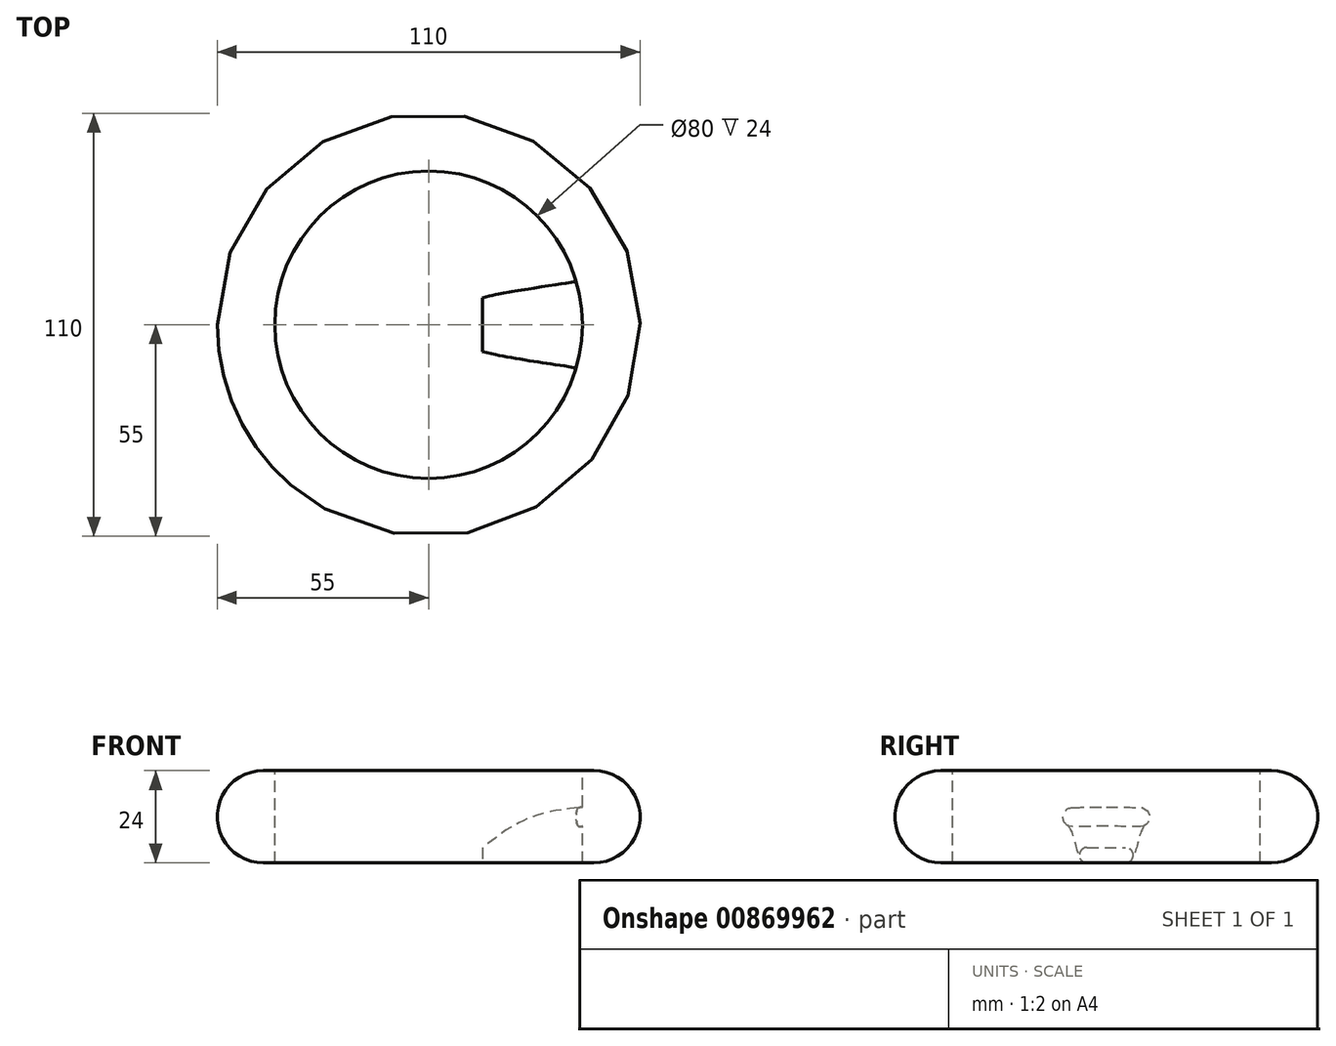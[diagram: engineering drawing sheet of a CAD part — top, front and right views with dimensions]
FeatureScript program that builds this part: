
annotation { "Feature Type Name" : "Feature", "Feature Type Description" : "" }
export const myFeature = defineFeature(function(context is Context, id is Id, definition is map)
    precondition{}
    {
        {
            var Q0;
            Q0=qCreatedBy(makeId("Top.planeOp"),FACE);
            var sketch = newSketch(context, id + "F0", { "sketchPlane" : qUnion([Q0])});
            skCircle(sketch, "E0", {"center": v(0, 0) * mm, "radius": 40 * mm});
            skSolve(sketch);
        }
        {
            var Q0;
            Q0=qCreatedBy(makeId("Front.planeOp"),FACE);
            var sketch = newSketch(context, id + "F1", { "sketchPlane" : qUnion([Q0])});
            skArc(sketch, "E1", {"start": v(-43, 12) * mm, "mid": v(-55, 0) * mm, "end": v(-43, -12) * mm});
            skLineSegment(sketch, "E2", {"start": v(-43, 12) * mm, "end": v(-40, 12) * mm});
            skLineSegment(sketch, "E3", {"start": v(-43, -12) * mm, "end": v(-40, -12) * mm});
            skLineSegment(sketch, "E4", {"start": v(-40, 12) * mm, "end": v(-40, -12) * mm});
            skSolve(sketch);
        }
        {
            var Q0;
            Q0=makeQuery(id+"F1.imprint","IMPRINT",FACE,{"disambiguationData":[TD([[makeQuery(id+"F1.imprint","IMPRINT",EDGE,{"derivedFrom":sQuery(id+"F1.wireOp",EDGE,"E1")}),1.0]])]});
            var Q1;
            Q1=sQuery(id+"F0.wireOp",EDGE,"E0");
            sweep(context, id + "F2", {"profiles" : qUnion([Q0]), "path" : qUnion([Q1])});
        }
        {
            var Q0;
            Q0=qCreatedBy(makeId("Right.planeOp"),FACE);
            cPlane(context, id + "F3", {"entities" : qUnion([Q0]), "cplaneType" : CPlaneType.OFFSET, "offset" : 40 * mm, "width" : 150 * mm, "height" : 150 * mm});
        }
        {
            var Q0;
            Q0=qCreatedBy(id+"F3.planeOp",FACE);
            var sketch = newSketch(context, id + "F4", { "sketchPlane" : qUnion([Q0])});
            skLineSegment(sketch, "E5", {"start": v(-9, 0) * mm, "end": v(9, 0) * mm});
            skArc(sketch, "E6.0.startCap", {"start": v(-9, -2.5) * mm, "mid": v(-11.5, 0) * mm, "end": v(-9, 2.5) * mm});
            skArc(sketch, "E6.0.endCap", {"start": v(9, 2.5) * mm, "mid": v(11.5, 0) * mm, "end": v(9, -2.5) * mm});
            skLineSegment(sketch, "E6.0.left", {"start": v(-9, 2.5) * mm, "end": v(9, 2.5) * mm});
            skLineSegment(sketch, "E6.0.right", {"start": v(-9, -2.5) * mm, "end": v(9, -2.5) * mm});
            skSolve(sketch);
        }
        {
            var Q0;
            Q0=qCreatedBy(makeId("Right.planeOp"),FACE);
            cPlane(context, id + "F5", {"entities" : qUnion([Q0]), "cplaneType" : CPlaneType.OFFSET, "offset" : 14 * mm, "width" : 150 * mm, "height" : 150 * mm});
        }
        {
            var Q0;
            Q0=qCreatedBy(id+"F5.planeOp",FACE);
            var sketch = newSketch(context, id + "F6", { "sketchPlane" : qUnion([Q0])});
            skLineSegment(sketch, "E7", {"start": v(-5, -10) * mm, "end": v(5, -10) * mm});
            skArc(sketch, "E8.0.startCap", {"start": v(-5, -12) * mm, "mid": v(-7, -10) * mm, "end": v(-5, -8) * mm});
            skArc(sketch, "E8.0.endCap", {"start": v(5, -8) * mm, "mid": v(7, -10) * mm, "end": v(5, -12) * mm});
            skLineSegment(sketch, "E8.0.left", {"start": v(-5, -8) * mm, "end": v(5, -8) * mm});
            skLineSegment(sketch, "E8.0.right", {"start": v(-5, -12) * mm, "end": v(5, -12) * mm});
            skSolve(sketch);
        }
        {
            var Q0;
            Q0=qCreatedBy(makeId("Front.planeOp"),FACE);
            var sketch = newSketch(context, id + "F7", { "sketchPlane" : qUnion([Q0])});
            skFitSpline(sketch, "E9", {"points": [v(14, -12) * mm, v(17.36, -10.57) * mm, v(19.73, -8.95) * mm, v(25.94, -5.3) * mm, v(34.78, -2.93) * mm, v(37.7, -2.65) * mm, v(40, -2.5) * mm], "startDerivative": vector(23.36, 2.46) * mm, "endDerivative": vector(25.77, 2.82) * mm});
            skSolve(sketch);
        }
        {
            var Q0;
            Q0 = qConstructionFilter(qBodyType(qCreatedBy(id + "F7" ,EDGE), BodyType.WIRE), ConstructionObject.NO);
            var Q2;
            Q2 = qSketchRegion(id + "F4", true);
            var Q3;
            Q3 = qSketchRegion(id + "F6", true);
            loft(context, id + "F8", {"operationType" : NewBodyOperationType.ADD, "addSections" : true, "spine" : qUnion([Q0]), "sectionCount" : 5, "sheetProfilesArray" : [{ "sheetProfileEntities" : qUnion([Q2]) }, { "sheetProfileEntities" : qUnion([Q3]) }]});
        }
    });
